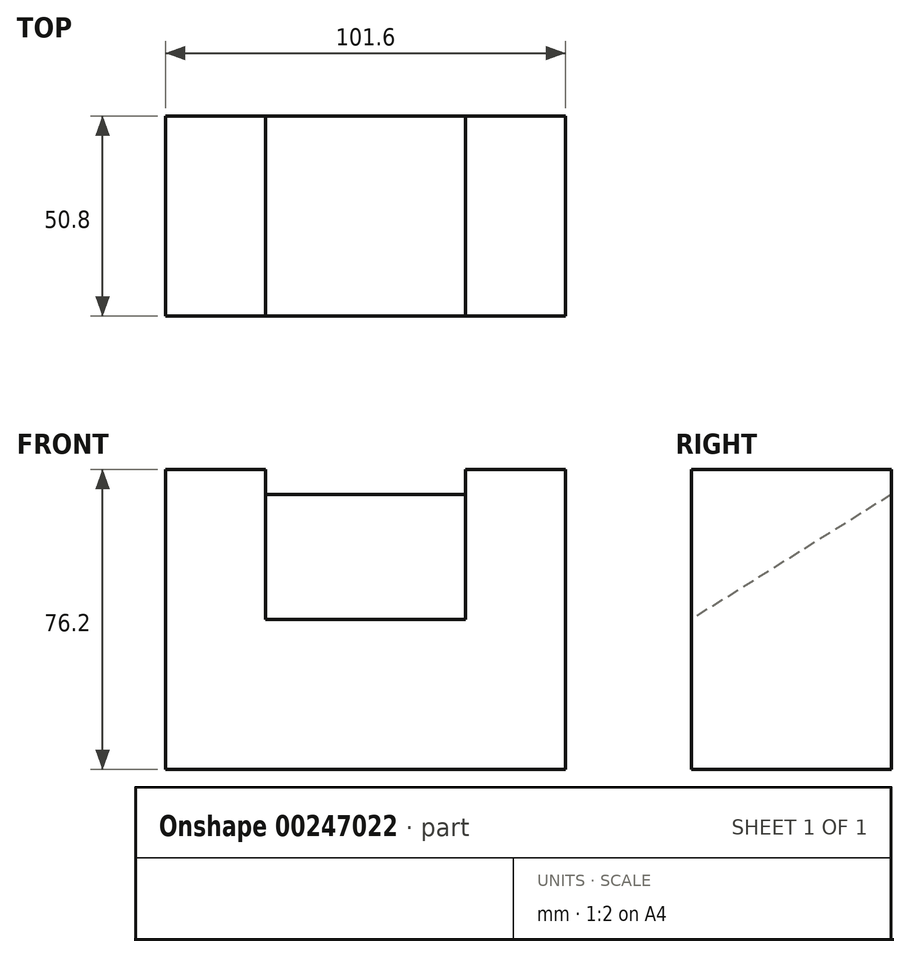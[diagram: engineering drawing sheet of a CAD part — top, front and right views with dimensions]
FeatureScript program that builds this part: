
annotation { "Feature Type Name" : "Feature", "Feature Type Description" : "" }
export const myFeature = defineFeature(function(context is Context, id is Id, definition is map)
    precondition{}
    {
        {
            var Q0;
            Q0=qCreatedBy(makeId("Front.planeOp"),FACE);
            var sketch = newSketch(context, id + "F0", { "sketchPlane" : qUnion([Q0])});
            skLineSegment(sketch, "E0", {"start": v(0, 0) * mm, "end": v(101.6, 0) * mm});
            skLineSegment(sketch, "E1", {"start": v(101.6, 0) * mm, "end": v(101.6, 76.2) * mm});
            skLineSegment(sketch, "E2", {"start": v(101.6, 76.2) * mm, "end": v(76.2, 76.2) * mm});
            skLineSegment(sketch, "E3", {"start": v(76.2, 76.2) * mm, "end": v(76.2, 38.1) * mm});
            skLineSegment(sketch, "E4", {"start": v(76.2, 38.1) * mm, "end": v(25.4, 38.1) * mm});
            skLineSegment(sketch, "E5", {"start": v(25.4, 38.1) * mm, "end": v(25.4, 76.2) * mm});
            skLineSegment(sketch, "E6", {"start": v(25.4, 76.2) * mm, "end": v(0, 76.2) * mm});
            skLineSegment(sketch, "E7", {"start": v(0, 76.2) * mm, "end": v(0, 0) * mm});
            skSolve(sketch);
        }
        {
            var Q0;
            Q0=makeQuery(id+"F0.imprint","IMPRINT",FACE,{"disambiguationData":[TD([[makeQuery(id+"F0.imprint","IMPRINT",EDGE,{"derivedFrom":sQuery(id+"F0.wireOp",EDGE,"E0")}),1.0]])]});
            extrude(context, id + "F1", {"entities" : qUnion([Q0]), "depth" : 50.8 * mm});
        }
        {
            var Q0;
            Q0=makeQuery(id+"F1.opExtrude","SWEPT_FACE",FACE,{"disambiguationData":[OSD([sQuery(id+"F0.wireOp",EDGE,"E5")])]});
            var sketch = newSketch(context, id + "F2", { "sketchPlane" : qUnion([Q0])});
            skLineSegment(sketch, "E8", {"start": v(0, 76.2) * mm, "end": v(0, 69.85) * mm});
            skLineSegment(sketch, "E9", {"start": v(0, 69.85) * mm, "end": v(-50.8, 38.1) * mm});
            skSolve(sketch);
        }
        {
            var Q0;
            {var subQ0=sQuery(id+"F2.wireOp",EDGE,"E9");Q0=makeQuery(id+"F2.imprint","IMPRINT",FACE,{"disambiguationData":[TD([[makeQuery(id+"F2.imprint","IMPRINT",EDGE,{"derivedFrom":subQ0}),1.0]])]});}
            extrude(context, id + "F3", {"entities" : qUnion([Q0]), "operationType" : NewBodyOperationType.ADD, "depth" : 50.8 * mm});
        }
    });
